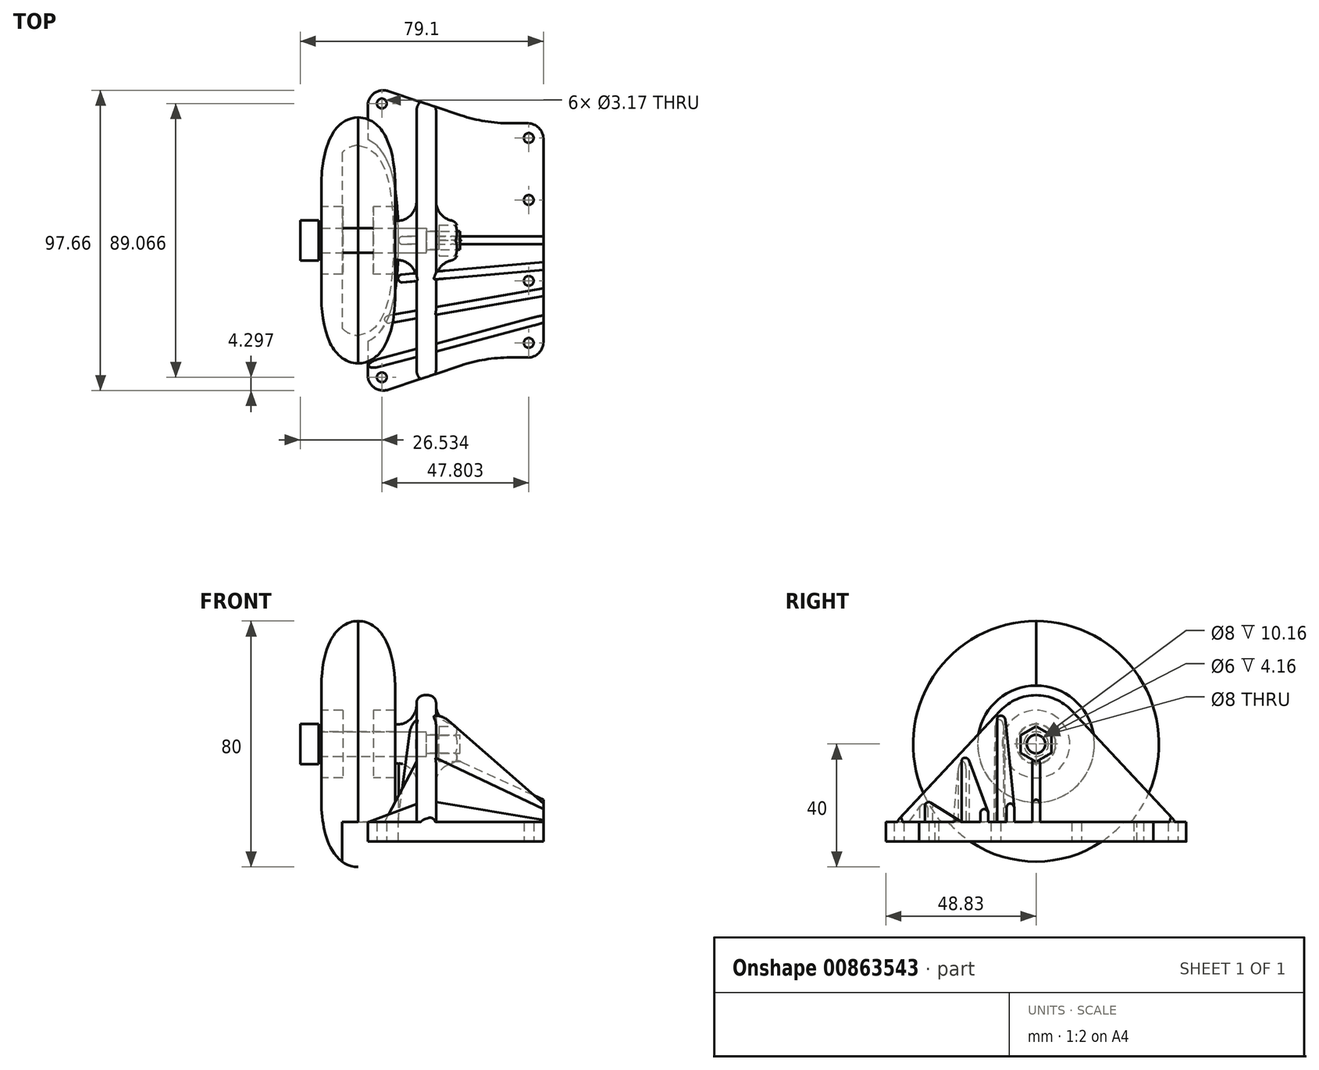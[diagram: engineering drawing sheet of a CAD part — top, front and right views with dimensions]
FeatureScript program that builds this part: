
annotation { "Feature Type Name" : "Feature", "Feature Type Description" : "" }
export const myFeature = defineFeature(function(context is Context, id is Id, definition is map)
    precondition{}
    {
        {
            var Q0;
            Q0=qCreatedBy(makeId("Top.planeOp"),FACE);
            var sketch = newSketch(context, id + "F0", { "sketchPlane" : qUnion([Q0])});
            skLineSegment(sketch, "E0", {"start": v(-19.05, 50.8) * mm, "end": v(-19.05, -50.8) * mm});
            skLineSegment(sketch, "E1", {"start": v(-19.05, -50.8) * mm, "end": v(19.05, -38.1) * mm});
            skLineSegment(sketch, "E2", {"start": v(38.1, -31.75) * mm, "end": v(38.1, 31.75) * mm});
            skLineSegment(sketch, "E3", {"start": v(19.05, 38.1) * mm, "end": v(-19.05, 50.8) * mm});
            skLineSegment(sketch, "E4", {"start": v(19.05, 38.1) * mm, "end": v(38.1, 38.1) * mm});
            skLineSegment(sketch, "E5", {"start": v(38.1, 38.1) * mm, "end": v(38.1, 31.75) * mm});
            skLineSegment(sketch, "E6", {"start": v(19.05, -38.1) * mm, "end": v(38.1, -38.1) * mm});
            skLineSegment(sketch, "E7", {"start": v(38.1, -38.1) * mm, "end": v(38.1, -31.75) * mm});
            skSolve(sketch);
        }
        {
            var Q0;
            Q0=makeQuery(id+"F0.imprint","IMPRINT",FACE,{"disambiguationData":[TD([[makeQuery(id+"F0.imprint","IMPRINT",EDGE,{"derivedFrom":sQuery(id+"F0.wireOp",EDGE,"E0")}),1.0]])]});
            extrude(context, id + "F1", {"entities" : qUnion([Q0]), "depth" : 6.35 * mm});
        }
        {
            var Q0;
            Q0=makeQuery(id+"F1.opExtrude","CAP_FACE",FACE,{"disambiguationData":[OSD([sQuery(id+"F0.wireOp",EDGE,"E0"),sQuery(id+"F0.wireOp",EDGE,"E1"),sQuery(id+"F0.wireOp",EDGE,"E2"),sQuery(id+"F0.wireOp",EDGE,"E3")])],"isStart":false});
            var sketch = newSketch(context, id + "F2", { "sketchPlane" : qUnion([Q0])});
            skLineSegment(sketch, "E8", {"start": v(-3.18, 45.5) * mm, "end": v(-3.17, -45.5) * mm});
            skLineSegment(sketch, "E9", {"start": v(-3.17, -45.5) * mm, "end": v(3.18, -43.4) * mm});
            skLineSegment(sketch, "E10", {"start": v(3.18, -43.4) * mm, "end": v(3.17, 43.4) * mm});
            skLineSegment(sketch, "E11", {"start": v(3.17, 43.4) * mm, "end": v(-3.18, 45.5) * mm});
            skSolve(sketch);
        }
        {
            var Q0;
            Q0=makeQuery(id+"F2.imprint","IMPRINT",FACE,{"disambiguationData":[TD([[makeQuery(id+"F2.imprint","IMPRINT",EDGE,{"derivedFrom":sQuery(id+"F2.wireOp",EDGE,"E8")}),1.0]])]});
            extrude(context, id + "F3", {"entities" : qUnion([Q0]), "operationType" : NewBodyOperationType.ADD, "depth" : 50.8 * mm, "offsetDistance" : 25.4 * mm});
        }
        {
            var Q0;
            Q0=qCreatedBy(makeId("Right.planeOp"),FACE);
            var sketch = newSketch(context, id + "F4", { "sketchPlane" : qUnion([Q0])});
            skArc(sketch, "E12", {"start": v(11.6, 42.6) * mm, "mid": v(0, 47.62) * mm, "end": v(-11.6, 42.6) * mm});
            skLineSegment(sketch, "E13", {"start": v(11.6, 42.6) * mm, "end": v(45.5, 6.35) * mm});
            skLineSegment(sketch, "E14", {"start": v(-11.6, 42.6) * mm, "end": v(-45.5, 6.35) * mm});
            skLineSegment(sketch, "E15", {"start": v(45.5, 6.35) * mm, "end": v(53.44, 6.35) * mm});
            skLineSegment(sketch, "E16", {"start": v(53.44, 6.35) * mm, "end": v(53.44, 59.99) * mm});
            skLineSegment(sketch, "E17", {"start": v(53.44, 59.99) * mm, "end": v(-55.67, 59.99) * mm});
            skLineSegment(sketch, "E18", {"start": v(-55.67, 59.99) * mm, "end": v(-55.67, 6.35) * mm});
            skLineSegment(sketch, "E19", {"start": v(-55.67, 6.35) * mm, "end": v(-45.5, 6.35) * mm});
            skSolve(sketch);
        }
        {
            var Q0;
            Q0=makeQuery(id+"F4.imprint","IMPRINT",FACE,{"disambiguationData":[TD([[makeQuery(id+"F4.imprint","IMPRINT",EDGE,{"derivedFrom":sQuery(id+"F4.wireOp",EDGE,"E12")}),-1.0]])]});
            extrude(context, id + "F5", {"entities" : qUnion([Q0]), "operationType" : NewBodyOperationType.REMOVE, "oppositeDirection" : true, "depth" : 7.11 * mm, "hasSecondDirection" : true, "secondDirectionOppositeDirection" : false, "secondDirectionDepth" : 4.06 * mm});
        }
        {
            var Q0;
            Q0=qCreatedBy(makeId("Right.planeOp"),FACE);
            var sketch = newSketch(context, id + "F6", { "sketchPlane" : qUnion([Q0])});
            skCircle(sketch, "E20", {"center": v(0, 513) * mm, "radius": 63.5 * mm});
            skCircle(sketch, "E21", {"center": v(0, 31.75) * mm, "radius": 6.35 * mm});
            skSolve(sketch);
        }
        {
            var Q0;
            Q0=qSketchRegion(id+"F6",true);
            extrude(context, id + "F7", {"entities" : qUnion([Q0]), "operationType" : NewBodyOperationType.ADD, "depth" : 10.16 * mm, "hasSecondDirection" : true, "secondDirectionOppositeDirection" : true, "secondDirectionDepth" : 10.16 * mm});
        }
        {
            var Q0;
            Q0=makeQuery(id+"F7.boolean.opBoolean","INTERSECT",EDGE,{"derivedFrom":[makeQuery(id+"F3.opExtrude","SWEPT_FACE",FACE,{"disambiguationData":[OSD([sQuery(id+"F2.wireOp",EDGE,"E8")])]}),makeQuery(id+"F7.opExtrude","SWEPT_FACE",FACE,{"disambiguationData":[OSD([sQuery(id+"F6.wireOp",EDGE,"E21")])]})]});
            var Q1;
            Q1=makeQuery(id+"F7.boolean.opBoolean","INTERSECT",EDGE,{"derivedFrom":[makeQuery(id+"F3.opExtrude","SWEPT_FACE",FACE,{"disambiguationData":[OSD([sQuery(id+"F2.wireOp",EDGE,"E10")])]}),makeQuery(id+"F7.opExtrude","SWEPT_FACE",FACE,{"disambiguationData":[OSD([sQuery(id+"F6.wireOp",EDGE,"E21")])]})]});
            fillet(context, id + "F8", {"entities" : qUnion([Q0, Q1]), "radius" : 6.35 * mm, "tangentPropagation" : true, "allowEdgeOverflow" : false});
        }
        {
            var Q0;
            Q0=makeQuery(id+"F5.boolean.opBoolean","INTERSECT",EDGE,{"derivedFrom":[makeQuery(id+"F3.opExtrude","SWEPT_FACE",FACE,{"disambiguationData":[OSD([sQuery(id+"F2.wireOp",EDGE,"E8")])]}),makeQuery(id+"F5.opExtrude","SWEPT_FACE",FACE,{"disambiguationData":[OSD([sQuery(id+"F4.wireOp",EDGE,"E13")])]})]});
            var Q1;
            Q1=makeQuery(id+"F5.boolean.opBoolean","INTERSECT",EDGE,{"derivedFrom":[makeQuery(id+"F3.opExtrude","SWEPT_FACE",FACE,{"disambiguationData":[OSD([sQuery(id+"F2.wireOp",EDGE,"E10")])]}),makeQuery(id+"F5.opExtrude","SWEPT_FACE",FACE,{"disambiguationData":[OSD([sQuery(id+"F4.wireOp",EDGE,"E13")])]})]});
            fillet(context, id + "F9", {"entities" : qUnion([Q0, Q1]), "radius" : 2.54 * mm, "tangentPropagation" : true, "allowEdgeOverflow" : false});
        }
        {
            var Q0;
            Q0=qCreatedBy(makeId("Right.planeOp"),FACE);
            var sketch = newSketch(context, id + "F10", { "sketchPlane" : qUnion([Q0])});
            skCircle(sketch, "E22", {"center": v(0, 31.75) * mm, "radius": 4 * mm});
            skSolve(sketch);
        }
        {
            var Q0;
            Q0=qSketchRegion(id+"F10",true);
            extrude(context, id + "F11", {"entities" : qUnion([Q0]), "operationType" : NewBodyOperationType.REMOVE, "oppositeDirection" : true, "depth" : 25.4 * mm});
        }
        {
            var Q0;
            Q0=makeQuery(id+"F7.opExtrude","CAP_FACE",FACE,{"disambiguationData":[OSD([sQuery(id+"F6.wireOp",EDGE,"E21")])],"isStart":false});
            var sketch = newSketch(context, id + "F12", { "sketchPlane" : qUnion([Q0])});
            skCircle(sketch, "E23.cCircle", {"center": v(0, 31.75) * mm, "radius": 5 * mm, "construction": true});
            skLineSegment(sketch, "E23.0", {"start": v(-5, 28.86) * mm, "end": v(-5, 34.64) * mm});
            skLineSegment(sketch, "E23.1", {"start": v(-5, 34.64) * mm, "end": v(0, 37.52) * mm});
            skLineSegment(sketch, "E23.2", {"start": v(0, 37.52) * mm, "end": v(5, 34.64) * mm});
            skLineSegment(sketch, "E23.3", {"start": v(5, 34.64) * mm, "end": v(5, 28.86) * mm});
            skLineSegment(sketch, "E23.4", {"start": v(5, 28.86) * mm, "end": v(0, 25.98) * mm});
            skLineSegment(sketch, "E23.5", {"start": v(0, 25.98) * mm, "end": v(-5, 28.86) * mm});
            skPoint(sketch, "E23.0.midPoint", {"position": v(-5, 31.75) * mm});
            skSolve(sketch);
        }
        {
            var Q0;
            Q0=makeQuery(id+"F12.imprint","IMPRINT",FACE,{"disambiguationData":[TD([[makeQuery(id+"F12.imprint","IMPRINT",EDGE,{"derivedFrom":sQuery(id+"F12.wireOp",EDGE,"E23.0")}),-1.0]])]});
            extrude(context, id + "F13", {"entities" : qUnion([Q0]), "operationType" : NewBodyOperationType.REMOVE, "oppositeDirection" : true, "depth" : 6 * mm});
        }
        {
            var Q0;
            Q0=makeQuery(id+"F7.opExtrude","CAP_EDGE",EDGE,{"disambiguationData":[OSD([sQuery(id+"F6.wireOp",EDGE,"E21")])],"isStart":false});
            fillet(context, id + "F14", {"entities" : qUnion([Q0]), "radius" : 2.54 * mm, "tangentPropagation" : true, "allowEdgeOverflow" : false});
        }
        {
            var Q0;
            Q0=makeQuery(id+"F7.opExtrude","SWEPT_BODY",BODY,{"disambiguationData":[OSD([sQuery(id+"F6.wireOp",EDGE,"E20")])]});
            deleteBodies(context, id + "F15", {"entities" : qUnion([Q0])});
        }
        {
            var Q0;
            Q0=qCreatedBy(makeId("Right.planeOp"),FACE);
            var sketch = newSketch(context, id + "F16", { "sketchPlane" : qUnion([Q0])});
            skCircle(sketch, "E24", {"center": v(0, 31.75) * mm, "radius": 3 * mm});
            skSolve(sketch);
        }
        {
            var Q0;
            Q0=qSketchRegion(id+"F16",true);
            extrude(context, id + "F17", {"entities" : qUnion([Q0]), "operationType" : NewBodyOperationType.REMOVE, "depth" : 25.4 * mm});
        }
        {
            var Q0;
            Q0=qCreatedBy(makeId("Front.planeOp"),FACE);
            var sketch = newSketch(context, id + "F18", { "sketchPlane" : qUnion([Q0])});
            skLineSegment(sketch, "E25", {"start": v(0, 31.75) * mm, "end": v(-46.53, 31.75) * mm, "construction": true});
            skLineSegment(sketch, "E26", {"start": v(-35, 35.75) * mm, "end": v(0, 35.75) * mm});
            skLineSegment(sketch, "E27", {"start": v(0, 35.75) * mm, "end": v(0, 34.75) * mm});
            skLineSegment(sketch, "E28", {"start": v(0, 34.75) * mm, "end": v(11, 34.75) * mm});
            skLineSegment(sketch, "E29", {"start": v(11, 34.75) * mm, "end": v(11, 31.75) * mm});
            skLineSegment(sketch, "E30", {"start": v(11, 31.75) * mm, "end": v(-41, 31.75) * mm});
            skLineSegment(sketch, "E31", {"start": v(-35, 35.75) * mm, "end": v(-35, 38.25) * mm});
            skLineSegment(sketch, "E32", {"start": v(-35, 38.25) * mm, "end": v(-41, 38.25) * mm});
            skLineSegment(sketch, "E33", {"start": v(-41, 38.25) * mm, "end": v(-41, 31.75) * mm});
            skSolve(sketch);
        }
        {
            var Q0;
            Q0=makeQuery(id+"F18.imprint","IMPRINT",FACE,{"disambiguationData":[TD([[makeQuery(id+"F18.imprint","IMPRINT",EDGE,{"derivedFrom":sQuery(id+"F18.wireOp",EDGE,"E26")}),-1.0]])]});
            var Q1;
            Q1=sQuery(id+"F18.wireOp",EDGE,"E25");
            revolve(context, id + "F19", {"entities" : qUnion([Q0]), "axis" : qUnion([Q1]), "revolveType" : RevolveType.FULL});
        }
        {
            var Q0;
            Q0=qCreatedBy(makeId("Front.planeOp"),FACE);
            var sketch = newSketch(context, id + "F20", { "sketchPlane" : qUnion([Q0])});
            skLineSegment(sketch, "E34", {"start": v(-51.26, 31.75) * mm, "end": v(0, 31.75) * mm});
            skLineSegment(sketch, "E35", {"start": v(-22.16, 31.75) * mm, "end": v(-22.16, 71.75) * mm, "construction": true});
            skPoint(sketch, "E36", {"position": v(-25.63, 31.75) * mm});
            skLineSegment(sketch, "E37", {"start": v(-22.16, 35.75) * mm, "end": v(-10.16, 35.75) * mm});
            skLineSegment(sketch, "E38", {"start": v(-10.16, 35.75) * mm, "end": v(-10.16, 50.75) * mm});
            skPoint(sketch, "E39.MirrorCS.2.internal.orphan", {"position": v(-34.16, 31.75) * mm});
            skPoint(sketch, "E39.MirrorCS.start.orphan", {"position": v(-22.16, 71.75) * mm});
            skPoint(sketch, "E40.2.internal.orphan", {"position": v(-10.16, 31.75) * mm});
            skFitSpline(sketch, "E41", {"points": [v(-22.16, 71.75) * mm, v(-10.16, 50.75) * mm], "startDerivative": vector(15.26, -0.07) * mm, "endDerivative": vector(1.21, -49.43) * mm});
            skPoint(sketch, "E42.MirrorCS.end.orphan", {"position": v(-34.16, 50.75) * mm});
            skFitSpline(sketch, "E43.MirrorCS", {"points": [v(-22.16, 71.75) * mm, v(-34.16, 50.75) * mm], "startDerivative": vector(-15.26, -0.07) * mm, "endDerivative": vector(-1.21, -49.43) * mm});
            skLineSegment(sketch, "E44.MirrorCS", {"start": v(-34.16, 35.75) * mm, "end": v(-34.16, 50.75) * mm});
            skLineSegment(sketch, "E45.MirrorCS", {"start": v(-22.16, 35.75) * mm, "end": v(-34.16, 35.75) * mm});
            skSolve(sketch);
        }
        {
            var Q0;
            Q0=makeQuery(id+"F20.imprint","IMPRINT",FACE,{"disambiguationData":[TD([[makeQuery(id+"F20.imprint","IMPRINT",EDGE,{"derivedFrom":sQuery(id+"F20.wireOp",EDGE,"E37")}),1.0]])]});
            var Q1;
            Q1=sQuery(id+"F20.wireOp",EDGE,"E34");
            revolve(context, id + "F21", {"entities" : qUnion([Q0]), "axis" : qUnion([Q1]), "revolveType" : RevolveType.FULL});
        }
        {
            var Q0;
            Q0=qCreatedBy(makeId("Front.planeOp"),FACE);
            var sketch = newSketch(context, id + "F22", { "sketchPlane" : qUnion([Q0])});
            skLineSegment(sketch, "E46", {"start": v(-62.06, 31.75) * mm, "end": v(0, 31.75) * mm, "construction": true});
            skLineSegment(sketch, "E47", {"start": v(-10.16, 31.75) * mm, "end": v(-10.16, 42.75) * mm});
            skLineSegment(sketch, "E48", {"start": v(-10.16, 42.75) * mm, "end": v(-17.16, 42.75) * mm});
            skLineSegment(sketch, "E49", {"start": v(-17.16, 42.75) * mm, "end": v(-17.16, 31.75) * mm});
            skLineSegment(sketch, "E50", {"start": v(-17.16, 31.75) * mm, "end": v(-10.16, 31.75) * mm});
            skLineSegment(sketch, "E51", {"start": v(-22.16, 31.75) * mm, "end": v(-22.16, 46.12) * mm, "construction": true});
            skLineSegment(sketch, "E52.MirrorCS", {"start": v(-34.16, 42.75) * mm, "end": v(-27.16, 42.75) * mm});
            skLineSegment(sketch, "E53.MirrorCS", {"start": v(-27.16, 42.75) * mm, "end": v(-27.16, 31.75) * mm});
            skLineSegment(sketch, "E54.MirrorCS", {"start": v(-34.16, 31.75) * mm, "end": v(-34.16, 42.75) * mm});
            skLineSegment(sketch, "E55", {"start": v(-27.16, 31.75) * mm, "end": v(-34.16, 31.75) * mm});
            skSolve(sketch);
        }
        {
            var Q0;
            Q0=qSketchRegion(id+"F22",true);
            var Q1;
            Q1=sQuery(id+"F22.wireOp",EDGE,"E46");
            revolve(context, id + "F23", {"entities" : qUnion([Q0]), "axis" : qUnion([Q1]), "revolveType" : RevolveType.FULL});
        }
        {
            var Q0;
            {var subQ0=sQuery(id+"F0.wireOp",EDGE,"E3");var subQ1=sQuery(id+"F0.wireOp",EDGE,"E1");var subQ2=sQuery(id+"F0.wireOp",EDGE,"E0");Q0=makeQuery(id+"F3.boolean.opBoolean","SPLIT",FACE,{"disambiguationData":[TD([makeQuery(id+"F1.opExtrude","SWEPT_FACE",FACE,{"disambiguationData":[OSD([subQ2])]})])],"derivedFrom":makeQuery(id+"F1.opExtrude","CAP_FACE",FACE,{"disambiguationData":[OSD([subQ2,subQ1,sQuery(id+"F0.wireOp",EDGE,"E2"),subQ0])],"isStart":false})});}
            var sketch = newSketch(context, id + "F24", { "sketchPlane" : qUnion([Q0])});
            skLineSegment(sketch, "E56", {"start": v(-19.05, 32.85) * mm, "end": v(-19.05, -32.85) * mm});
            skFitSpline(sketch, "E57.0", {"points": [v(-22.67, -33.39) * mm, v(-22.46, -33.43) * mm, v(-22.05, -33.49) * mm, v(-21.48, -33.49) * mm, v(-20.97, -33.44) * mm, v(-20.5, -33.35) * mm, v(-20.07, -33.24) * mm, v(-19.65, -33.1) * mm, v(-19.27, -32.95) * mm, v(-18.9, -32.79) * mm, v(-18.56, -32.62) * mm, v(-18.23, -32.43) * mm, v(-17.91, -32.24) * mm, v(-17.5, -31.97) * mm, v(-17.03, -31.62) * mm, v(-16.3, -31.03) * mm, v(-15.49, -30.22) * mm, v(-14.62, -29.2) * mm, v(-13.87, -28.1) * mm, v(-13.21, -26.98) * mm, v(-12.65, -25.84) * mm, v(-12.17, -24.7) * mm, v(-11.76, -23.55) * mm, v(-11.28, -22.02) * mm, v(-10.8, -20.12) * mm, v(-10.34, -17.83) * mm, v(-10, -15.56) * mm, v(-9.63, -12.57) * mm, v(-9.33, -8.85) * mm, v(-9.13, -4.4) * mm, v(-9.07, 0.02) * mm, v(-9.13, 4.46) * mm, v(-9.3, 8.17) * mm, v(-9.52, 11.16) * mm, v(-9.73, 13.4) * mm, v(-10, 15.66) * mm, v(-10.36, 17.92) * mm, v(-10.81, 20.2) * mm, v(-11.4, 22.47) * mm, v(-12.03, 24.37) * mm, v(-12.67, 25.89) * mm, v(-13.24, 27.03) * mm, v(-13.9, 28.15) * mm, v(-14.65, 29.23) * mm, v(-15.52, 30.26) * mm, v(-16.5, 31.2) * mm, v(-17.6, 32.06) * mm, v(-18.66, 32.7) * mm, v(-19.65, 33.11) * mm, v(-20.35, 33.32) * mm, v(-20.98, 33.44) * mm, v(-21.49, 33.49) * mm, v(-22.05, 33.48) * mm, v(-22.46, 33.43) * mm, v(-22.67, 33.39) * mm]});
            skPoint(sketch, "E58.trimOffspring.end.orphan", {"position": v(-22.16, 30.9) * mm});
            skPoint(sketch, "E59.start.orphan", {"position": v(-22.16, -30.9) * mm});
            skLineSegment(sketch, "E60", {"start": v(-19.05, 32.85) * mm, "end": v(-27.36, 32.85) * mm});
            skLineSegment(sketch, "E61", {"start": v(-27.36, 32.85) * mm, "end": v(-27.36, -33.81) * mm});
            skLineSegment(sketch, "E62", {"start": v(-27.36, -33.81) * mm, "end": v(-19.05, -32.85) * mm});
            skSolve(sketch);
        }
        {
            var Q0;
            Q0=makeQuery(id+"F24.imprint","IMPRINT",FACE,{"disambiguationData":[TD([[makeQuery(id+"F24.imprint","IMPRINT",EDGE,{"derivedFrom":sQuery(id+"F24.wireOp",EDGE,"E56")}),-1.0]])]});
            var Q1;
            Q1=makeQuery(id+"F24.imprint","IMPRINT",FACE,{"disambiguationData":[TD([[makeQuery(id+"F24.imprint","IMPRINT",EDGE,{"derivedFrom":sQuery(id+"F24.wireOp",EDGE,"E56")}),1.0]])]});
            extrude(context, id + "F25", {"entities" : qUnion([Q0, Q1]), "operationType" : NewBodyOperationType.REMOVE, "oppositeDirection" : true, "depth" : 25.4 * mm});
        }
        {
            var Q0;
            Q0=qCreatedBy(makeId("Front.planeOp"),FACE);
            var sketch = newSketch(context, id + "F26", { "sketchPlane" : qUnion([Q0])});
            skLineSegment(sketch, "E63", {"start": v(-9.01, 6.35) * mm, "end": v(-9.01, 26.67) * mm});
            skLineSegment(sketch, "E64", {"start": v(-9.01, 26.67) * mm, "end": v(9.85, 26.67) * mm});
            skLineSegment(sketch, "E65", {"start": v(9.85, 26.67) * mm, "end": v(53.98, 6.35) * mm});
            skLineSegment(sketch, "E66", {"start": v(53.98, 6.35) * mm, "end": v(-9.01, 6.35) * mm});
            skSolve(sketch);
        }
        {
            var Q0;
            Q0=makeQuery(id+"F26.imprint","IMPRINT",FACE,{"disambiguationData":[TD([[makeQuery(id+"F26.imprint","IMPRINT",EDGE,{"derivedFrom":sQuery(id+"F26.wireOp",EDGE,"E63")}),-1.0]])]});
            extrude(context, id + "F27", {"entities" : qUnion([Q0]), "operationType" : NewBodyOperationType.ADD, "depth" : 1.27 * mm, "hasSecondDirection" : true, "secondDirectionOppositeDirection" : true, "secondDirectionDepth" : 1.27 * mm});
        }
        {
            var Q0;
            Q0=qCreatedBy(makeId("Top.planeOp"),FACE);
            var sketch = newSketch(context, id + "F28", { "sketchPlane" : qUnion([Q0])});
            skLineSegment(sketch, "E67", {"start": v(-23.06, -52.14) * mm, "end": v(133.35, 0) * mm});
            skLineSegment(sketch, "E68", {"start": v(133.35, 0) * mm, "end": v(-28.84, 0) * mm});
            skLineSegment(sketch, "E69", {"start": v(133.35, 0) * mm, "end": v(-37.86, -14.98) * mm});
            skLineSegment(sketch, "E70", {"start": v(133.35, 0) * mm, "end": v(-37.54, -30.13) * mm});
            skLineSegment(sketch, "E71", {"start": v(133.35, 0) * mm, "end": v(-45.99, -48.05) * mm});
            skSolve(sketch);
        }
        {
            var Q0;
            Q0=sQuery(id+"F28.wireOp",EDGE,"E69");
            cPlane(context, id + "F29", {"entities" : qUnion([Q0]), "cplaneType" : CPlaneType.LINE_ANGLE, "offset" : 25.4 * mm, "angle" : 0 * degree, "width" : 152.4 * mm, "height" : 152.4 * mm});
        }
        {
            var Q0;
            Q0=qCreatedBy(id+"F29.planeOp",FACE);
            var sketch = newSketch(context, id + "F30", { "sketchPlane" : qUnion([Q0])});
            skLineSegment(sketch, "E72", {"start": v(6.12, 39.44) * mm, "end": v(44.18, 6.35) * mm});
            skLineSegment(sketch, "E73", {"start": v(44.18, 6.35) * mm, "end": v(-10.24, 6.35) * mm});
            skLineSegment(sketch, "E74", {"start": v(-10.24, 6.35) * mm, "end": v(-6.43, 35.5) * mm});
            skPoint(sketch, "E75.visualSharp", {"position": v(-6.52, 34.82) * mm});
            skArc(sketch, "E75.filletArc", {"start": v(-3.16, 40.25) * mm, "mid": v(-5.37, 38.27) * mm, "end": v(-6.43, 35.5) * mm});
            skLineSegment(sketch, "E76", {"start": v(1.95, 41) * mm, "end": v(0.46, 41) * mm});
            skLineSegment(sketch, "E77", {"start": v(0.46, 41) * mm, "end": v(-3.16, 40.25) * mm});
            skPoint(sketch, "E78.visualSharp", {"position": v(4.32, 41) * mm});
            skArc(sketch, "E78.filletArc", {"start": v(6.12, 39.44) * mm, "mid": v(4.17, 40.6) * mm, "end": v(1.95, 41) * mm});
            skSolve(sketch);
        }
        {
            var Q0;
            Q0=makeQuery(id+"F30.imprint","IMPRINT",FACE,{"disambiguationData":[TD([[makeQuery(id+"F30.imprint","IMPRINT",EDGE,{"derivedFrom":sQuery(id+"F30.wireOp",EDGE,"E72")}),-1.0]])]});
            extrude(context, id + "F31", {"entities" : qUnion([Q0]), "operationType" : NewBodyOperationType.ADD, "depth" : 1.27 * mm, "hasSecondDirection" : true, "secondDirectionOppositeDirection" : true, "secondDirectionDepth" : 1.27 * mm});
        }
        {
            var Q0;
            Q0=sQuery(id+"F28.wireOp",EDGE,"E70");
            cPlane(context, id + "F32", {"entities" : qUnion([Q0]), "cplaneType" : CPlaneType.LINE_ANGLE, "offset" : 25.4 * mm, "angle" : 0 * degree, "width" : 152.4 * mm, "height" : 152.4 * mm});
        }
        {
            var Q0;
            Q0=qCreatedBy(id+"F32.planeOp",FACE);
            var sketch = newSketch(context, id + "F33", { "sketchPlane" : qUnion([Q0])});
            skLineSegment(sketch, "E79", {"start": v(43.53, 6.35) * mm, "end": v(-17.77, 6.35) * mm});
            skLineSegment(sketch, "E80", {"start": v(-17.77, 6.35) * mm, "end": v(-6.14, 28.2) * mm});
            skLineSegment(sketch, "E81", {"start": v(-6.14, 28.2) * mm, "end": v(-2.9, 28.2) * mm});
            skLineSegment(sketch, "E82", {"start": v(-2.9, 28.2) * mm, "end": v(43.53, 6.35) * mm});
            skSolve(sketch);
        }
        {
            var Q0;
            Q0=makeQuery(id+"F33.imprint","IMPRINT",FACE,{"disambiguationData":[TD([[makeQuery(id+"F33.imprint","IMPRINT",EDGE,{"derivedFrom":sQuery(id+"F33.wireOp",EDGE,"E79")}),-1.0]])]});
            extrude(context, id + "F34", {"entities" : qUnion([Q0]), "operationType" : NewBodyOperationType.ADD, "depth" : 1.27 * mm, "hasSecondDirection" : true, "secondDirectionOppositeDirection" : true, "secondDirectionDepth" : 1.27 * mm});
        }
        {
            var Q0;
            Q0=sQuery(id+"F28.wireOp",EDGE,"E71");
            cPlane(context, id + "F35", {"entities" : qUnion([Q0]), "cplaneType" : CPlaneType.LINE_ANGLE, "offset" : 25.4 * mm, "angle" : 0 * degree, "width" : 152.4 * mm, "height" : 152.4 * mm});
        }
        {
            var Q0;
            Q0=qCreatedBy(id+"F35.planeOp",FACE);
            var sketch = newSketch(context, id + "F36", { "sketchPlane" : qUnion([Q0])});
            skLineSegment(sketch, "E83", {"start": v(-28.7, 6.35) * mm, "end": v(-10.05, 13.08) * mm});
            skLineSegment(sketch, "E84", {"start": v(-10.05, 13.08) * mm, "end": v(-7.43, 13.08) * mm});
            skLineSegment(sketch, "E85", {"start": v(-7.43, 13.08) * mm, "end": v(34.6, 6.35) * mm});
            skLineSegment(sketch, "E86", {"start": v(34.6, 6.35) * mm, "end": v(-28.7, 6.35) * mm});
            skSolve(sketch);
        }
        {
            var Q0;
            Q0=makeQuery(id+"F36.imprint","IMPRINT",FACE,{"disambiguationData":[TD([[makeQuery(id+"F36.imprint","IMPRINT",EDGE,{"derivedFrom":sQuery(id+"F36.wireOp",EDGE,"E83")}),-1.0]])]});
            extrude(context, id + "F37", {"entities" : qUnion([Q0]), "operationType" : NewBodyOperationType.ADD, "depth" : 1.27 * mm, "hasSecondDirection" : true, "secondDirectionOppositeDirection" : true, "secondDirectionDepth" : 1.27 * mm});
        }
        {
            var Q0;
            Q0=makeQuery(id+"F1.opExtrude","SWEPT_EDGE",EDGE,{"disambiguationData":[OSD([sQuery(id+"F0.wireOp",EDGE,"E0"),sQuery(id+"F0.wireOp",EDGE,"E3")])]});
            var Q1;
            Q1=makeQuery(id+"F1.opExtrude","SWEPT_EDGE",EDGE,{"disambiguationData":[OSD([sQuery(id+"F0.wireOp",EDGE,"E0"),sQuery(id+"F0.wireOp",EDGE,"E1")])]});
            fillet(context, id + "F38", {"entities" : qUnion([Q0, Q1]), "radius" : 5.08 * mm, "tangentPropagation" : true, "allowEdgeOverflow" : false});
        }
        {
            var Q0;
            Q0=qCreatedBy(makeId("Top.planeOp"),FACE);
            var sketch = newSketch(context, id + "F39", { "sketchPlane" : qUnion([Q0])});
            skCircle(sketch, "E87", {"center": v(-14.47, 44.53) * mm, "radius": 1.59 * mm});
            skCircle(sketch, "E88", {"center": v(33.34, 33.34) * mm, "radius": 1.59 * mm});
            skCircle(sketch, "E89", {"center": v(33.34, 13.15) * mm, "radius": 1.59 * mm});
            skLineSegment(sketch, "E90", {"start": v(-47.45, 0) * mm, "end": v(55.73, 0) * mm, "construction": true});
            skCircle(sketch, "E91.MirrorC", {"center": v(-14.47, -44.53) * mm, "radius": 1.59 * mm});
            skCircle(sketch, "E92.MirrorC", {"center": v(33.34, -33.34) * mm, "radius": 1.59 * mm});
            skCircle(sketch, "E93.MirrorC", {"center": v(33.34, -13.15) * mm, "radius": 1.59 * mm});
            skSolve(sketch);
        }
        {
            var Q0;
            Q0=qSketchRegion(id+"F39",true);
            extrude(context, id + "F40", {"entities" : qUnion([Q0]), "operationType" : NewBodyOperationType.REMOVE, "depth" : 25.4 * mm});
        }
        {
            var Q0;
            Q0=qCreatedBy(makeId("Top.planeOp"),FACE);
            var sketch = newSketch(context, id + "F41", { "sketchPlane" : qUnion([Q0])});
            skLineSegment(sketch, "E94", {"start": v(38.1, 38.22) * mm, "end": v(38.1, -45.48) * mm});
            skLineSegment(sketch, "E95", {"start": v(38.1, -45.48) * mm, "end": v(62.17, -45.48) * mm});
            skLineSegment(sketch, "E96", {"start": v(62.17, -45.48) * mm, "end": v(51.52, 37.8) * mm});
            skLineSegment(sketch, "E97", {"start": v(51.52, 37.8) * mm, "end": v(38.1, 38.22) * mm});
            skSolve(sketch);
        }
        {
            var Q0;
            Q0=makeQuery(id+"F41.imprint","IMPRINT",FACE,{"disambiguationData":[TD([[makeQuery(id+"F41.imprint","IMPRINT",EDGE,{"derivedFrom":sQuery(id+"F41.wireOp",EDGE,"E94")}),1.0]])]});
            extrude(context, id + "F42", {"entities" : qUnion([Q0]), "operationType" : NewBodyOperationType.REMOVE, "depth" : 22.35 * mm});
        }
        {
            var Q0;
            Q0=makeQuery(id+"F1.opExtrude","SWEPT_EDGE",EDGE,{"disambiguationData":[OSD([sQuery(id+"F0.wireOp",EDGE,"E6"),sQuery(id+"F0.wireOp",EDGE,"E7")])]});
            var Q1;
            Q1=makeQuery(id+"F1.opExtrude","SWEPT_EDGE",EDGE,{"disambiguationData":[OSD([sQuery(id+"F0.wireOp",EDGE,"E4"),sQuery(id+"F0.wireOp",EDGE,"E5")])]});
            fillet(context, id + "F43", {"entities" : qUnion([Q0, Q1]), "radius" : 5.08 * mm, "tangentPropagation" : true, "allowEdgeOverflow" : false});
        }
        {
            var Q0;
            Q0=makeQuery(id+"F1.opExtrude","SWEPT_EDGE",EDGE,{"disambiguationData":[OSD([sQuery(id+"F0.wireOp",EDGE,"E3"),sQuery(id+"F0.wireOp",EDGE,"E4")])]});
            var Q1;
            Q1=makeQuery(id+"F1.opExtrude","SWEPT_EDGE",EDGE,{"disambiguationData":[OSD([sQuery(id+"F0.wireOp",EDGE,"E1"),sQuery(id+"F0.wireOp",EDGE,"E6")])]});
            fillet(context, id + "F44", {"entities" : qUnion([Q0, Q1]), "radius" : 50.8 * mm, "tangentPropagation" : true, "allowEdgeOverflow" : false});
        }
        {
            var Q0;
            Q0=makeQuery(id+"F27.opExtrude","CAP_EDGE",EDGE,{"disambiguationData":[OSD([sQuery(id+"F26.wireOp",EDGE,"E65")])],"isStart":false});
            var Q1;
            Q1=makeQuery(id+"F27.opExtrude","CAP_EDGE",EDGE,{"disambiguationData":[OSD([sQuery(id+"F26.wireOp",EDGE,"E65")])],"isStart":true});
            var Q2;
            Q2=makeQuery(id+"F31.opExtrude","CAP_EDGE",EDGE,{"disambiguationData":[OSD([sQuery(id+"F30.wireOp",EDGE,"E72")])],"isStart":true});
            var Q3;
            Q3=makeQuery(id+"F31.opExtrude","CAP_EDGE",EDGE,{"disambiguationData":[OSD([sQuery(id+"F30.wireOp",EDGE,"E72")])],"isStart":false});
            var Q4;
            Q4=makeQuery(id+"F31.opExtrude","CAP_EDGE",EDGE,{"disambiguationData":[OSD([sQuery(id+"F30.wireOp",EDGE,"E75.filletArc")])],"isStart":false});
            var Q5;
            Q5=makeQuery(id+"F31.opExtrude","CAP_EDGE",EDGE,{"disambiguationData":[OSD([sQuery(id+"F30.wireOp",EDGE,"E75.filletArc")])],"isStart":true});
            var Q6;
            Q6=makeQuery(id+"F34.opExtrude","CAP_EDGE",EDGE,{"disambiguationData":[OSD([sQuery(id+"F33.wireOp",EDGE,"E82")])],"isStart":false});
            var Q7;
            Q7=makeQuery(id+"F34.opExtrude","CAP_EDGE",EDGE,{"disambiguationData":[OSD([sQuery(id+"F33.wireOp",EDGE,"E82")])],"isStart":true});
            var Q8;
            Q8=makeQuery(id+"F34.opExtrude","CAP_EDGE",EDGE,{"disambiguationData":[OSD([sQuery(id+"F33.wireOp",EDGE,"E80")])],"isStart":false});
            var Q9;
            Q9=makeQuery(id+"F34.opExtrude","CAP_EDGE",EDGE,{"disambiguationData":[OSD([sQuery(id+"F33.wireOp",EDGE,"E80")])],"isStart":true});
            var Q10;
            Q10=makeQuery(id+"F37.opExtrude","CAP_EDGE",EDGE,{"disambiguationData":[OSD([sQuery(id+"F36.wireOp",EDGE,"E83")])],"isStart":false});
            var Q11;
            Q11=makeQuery(id+"F37.opExtrude","CAP_EDGE",EDGE,{"disambiguationData":[OSD([sQuery(id+"F36.wireOp",EDGE,"E83")])],"isStart":true});
            var Q12;
            Q12=makeQuery(id+"F37.opExtrude","CAP_EDGE",EDGE,{"disambiguationData":[OSD([sQuery(id+"F36.wireOp",EDGE,"E85")])],"isStart":false});
            var Q13;
            Q13=makeQuery(id+"F37.opExtrude","CAP_EDGE",EDGE,{"disambiguationData":[OSD([sQuery(id+"F36.wireOp",EDGE,"E85")])],"isStart":true});
            var Q14;
            Q14=makeQuery(id+"FzpeDoiq8tc86xp_5.1.F31.opExtrude","CAP_EDGE",EDGE,{"disambiguationData":[OSD([sQuery(id+"F30.wireOp",EDGE,"E72")])],"isStart":true});
            var Q15;
            Q15=makeQuery(id+"FzpeDoiq8tc86xp_5.1.F31.opExtrude","CAP_EDGE",EDGE,{"disambiguationData":[OSD([sQuery(id+"F30.wireOp",EDGE,"E72")])],"isStart":false});
            var Q16;
            Q16=makeQuery(id+"FzpeDoiq8tc86xp_5.1.F34.opExtrude","CAP_EDGE",EDGE,{"disambiguationData":[OSD([sQuery(id+"F33.wireOp",EDGE,"E82")])],"isStart":true});
            var Q17;
            Q17=makeQuery(id+"FzpeDoiq8tc86xp_5.1.F34.opExtrude","CAP_EDGE",EDGE,{"disambiguationData":[OSD([sQuery(id+"F33.wireOp",EDGE,"E82")])],"isStart":false});
            var Q18;
            Q18=makeQuery(id+"FzpeDoiq8tc86xp_5.1.F37.opExtrude","CAP_EDGE",EDGE,{"disambiguationData":[OSD([sQuery(id+"F36.wireOp",EDGE,"E85")])],"isStart":true});
            var Q19;
            Q19=makeQuery(id+"FzpeDoiq8tc86xp_5.1.F37.opExtrude","CAP_EDGE",EDGE,{"disambiguationData":[OSD([sQuery(id+"F36.wireOp",EDGE,"E85")])],"isStart":false});
            var Q20;
            Q20=makeQuery(id+"F27.opExtrude","CAP_EDGE",EDGE,{"disambiguationData":[OSD([sQuery(id+"F26.wireOp",EDGE,"E63")])],"isStart":false});
            var Q21;
            Q21=makeQuery(id+"FzpeDoiq8tc86xp_5.1.F31.opExtrude","CAP_EDGE",EDGE,{"disambiguationData":[OSD([sQuery(id+"F30.wireOp",EDGE,"E74")])],"isStart":true});
            var Q22;
            Q22=makeQuery(id+"FzpeDoiq8tc86xp_5.1.F31.opExtrude","CAP_EDGE",EDGE,{"disambiguationData":[OSD([sQuery(id+"F30.wireOp",EDGE,"E74")])],"isStart":false});
            var Q23;
            Q23=makeQuery(id+"FzpeDoiq8tc86xp_5.1.F34.opExtrude","CAP_EDGE",EDGE,{"disambiguationData":[OSD([sQuery(id+"F33.wireOp",EDGE,"E80")])],"isStart":true});
            var Q24;
            Q24=makeQuery(id+"FzpeDoiq8tc86xp_5.1.F34.opExtrude","CAP_EDGE",EDGE,{"disambiguationData":[OSD([sQuery(id+"F33.wireOp",EDGE,"E80")])],"isStart":false});
            var Q25;
            Q25=makeQuery(id+"FzpeDoiq8tc86xp_5.1.F37.opExtrude","CAP_EDGE",EDGE,{"disambiguationData":[OSD([sQuery(id+"F36.wireOp",EDGE,"E83")])],"isStart":true});
            var Q26;
            Q26=makeQuery(id+"F27.opExtrude","CAP_EDGE",EDGE,{"disambiguationData":[OSD([sQuery(id+"F26.wireOp",EDGE,"E63")])],"isStart":true});
            fillet(context, id + "F45", {"entities" : qUnion([Q0, Q1, Q2, Q3, Q4, Q5, Q6, Q7, Q8, Q9, Q10, Q11, Q12, Q13, Q14, Q15, Q16, Q17, Q18, Q19, Q20, Q21, Q22, Q23, Q24, Q25, Q26]), "radius" : 1.27 * mm, "tangentPropagation" : true, "allowEdgeOverflow" : false});
        }
        {
            var Q0;
            Q0=makeQuery(id+"F13.boolean.opBoolean","COPY",FACE,{"derivedFrom":makeQuery(id+"F13.opExtrude","CAP_FACE",FACE,{"disambiguationData":[OSD([sQuery(id+"F12.wireOp",EDGE,"E23.0"),sQuery(id+"F12.wireOp",EDGE,"E23.1"),sQuery(id+"F12.wireOp",EDGE,"E23.2"),sQuery(id+"F12.wireOp",EDGE,"E23.3"),sQuery(id+"F12.wireOp",EDGE,"E23.4"),sQuery(id+"F12.wireOp",EDGE,"E23.5")])],"isStart":false})});
            var sketch = newSketch(context, id + "F46", { "sketchPlane" : qUnion([Q0])});
            skLineSegment(sketch, "E98", {"start": v(-5, 28.86) * mm, "end": v(0, 25.98) * mm});
            skLineSegment(sketch, "E99", {"start": v(0, 25.98) * mm, "end": v(5, 28.86) * mm});
            skLineSegment(sketch, "E100", {"start": v(5, 28.86) * mm, "end": v(0, 27.7) * mm});
            skLineSegment(sketch, "E101", {"start": v(0, 27.7) * mm, "end": v(-5, 28.86) * mm});
            skSolve(sketch);
        }
        {
            var Q0;
            Q0 = qSketchRegion(id + "F46", true);
            extrude(context, id + "F47", {"entities" : qUnion([Q0]), "operationType" : NewBodyOperationType.REMOVE, "endBound" : BoundingType.THROUGH_ALL, "depth" : 25.4 * mm, "offsetDistance" : 25.4 * mm});
        }
    });
